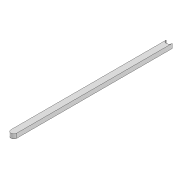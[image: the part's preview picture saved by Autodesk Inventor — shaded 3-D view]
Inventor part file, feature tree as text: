
AUTODESK INVENTOR PART (.ipt)
format: ipt  version: 2022 (Build 260153000, 153)  size: 81,408 bytes
history: native  units: mm
features: extrude x1, sketch x1
ambient origin geometry x8: Origin, YZ Plane, XZ Plane, XY Plane, X Axis, Y Axis, Z Axis, Center Point
bodies: Solid1 (feature_tree)
feature tree (2):
  extrude  "Extrusion1"  Depth=8.0mm
  sketch  "Sketch1"  dims[d0=210.0mm d1=8.0mm d2=6.0mm d3=0.0mm]
